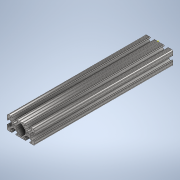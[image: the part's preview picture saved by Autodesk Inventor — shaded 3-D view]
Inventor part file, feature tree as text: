
AUTODESK INVENTOR PART (.ipt)
format: ipt  version: 2020 (Build 240168000, 168)  size: 343,040 bytes
history: native  units: in
note: dims shown in document units (in); Inventor stores cm internally (conversion verified against a paired STEP export)
features: sketch x2, extrude x1
ambient origin geometry x8: Origin, YZ Plane, XZ Plane, XY Plane, X Axis, Y Axis, Z Axis, Center Point
bodies: Solid1 (feature_tree)
feature tree (3):
  extrude  "Extrusion1"  [1 undecoded]
  sketch  "Sketch2"
  sketch  "Sketch1"  dims[d0=10.0in d1=0.0in]
note: 1 required parameter value undecoded (feature->parameter linkage not recoverable at this tier; creation-order binding heuristic only, values carry confidence <= 0.55)
